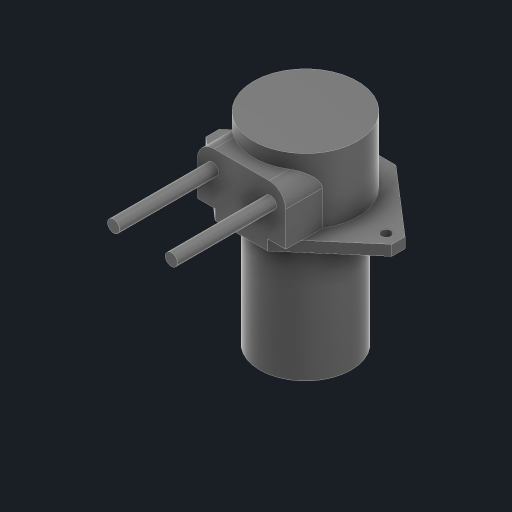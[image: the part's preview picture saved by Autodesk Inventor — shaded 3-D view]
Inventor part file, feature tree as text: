
AUTODESK INVENTOR PART (.ipt)
format: ipt  version: 2023.1 (Build 271208000, 208)  size: 176,640 bytes
history: native  units: mm
features: extrude x5, sketch x2, fillet x1
ambient origin geometry x8: Origin, YZ Plane, XZ Plane, XY Plane, X Axis, Y Axis, Z Axis, Center Point
bodies: Solid1 (feature_tree)
feature tree (8):
  sketch  "Sketch1"  dims[d0=56.36mm d1=38.78mm]
  extrude  "Extrusion1"  Depth=38.78mm
  extrude  "Extrusion2"  Depth=5.0mm
  extrude  "Extrusion3"  Depth=5.0mm
  extrude  "Extrusion4"  Depth=26.77mm
  extrude  "Extrusion5"  Depth=5.0mm
  fillet  "Fillet1"  Radius=3.75mm
  sketch  "Sketch2"  dims[d2=4.0mm d3=16.0mm d4=31.5mm d5=26.77mm d6=3.0mm d7=3.75mm d8=27.72mm d9=3.16mm d10=0.0mm d11=23.0mm d12=0.0mm d13=15.5mm d14=0.0mm d15=38.0mm d16=0.0mm d17=5.5mm d18=17.5mm d19=3.7mm d20=3.7mm d21=30.0mm d22=0.0mm d23=5.0mm]
